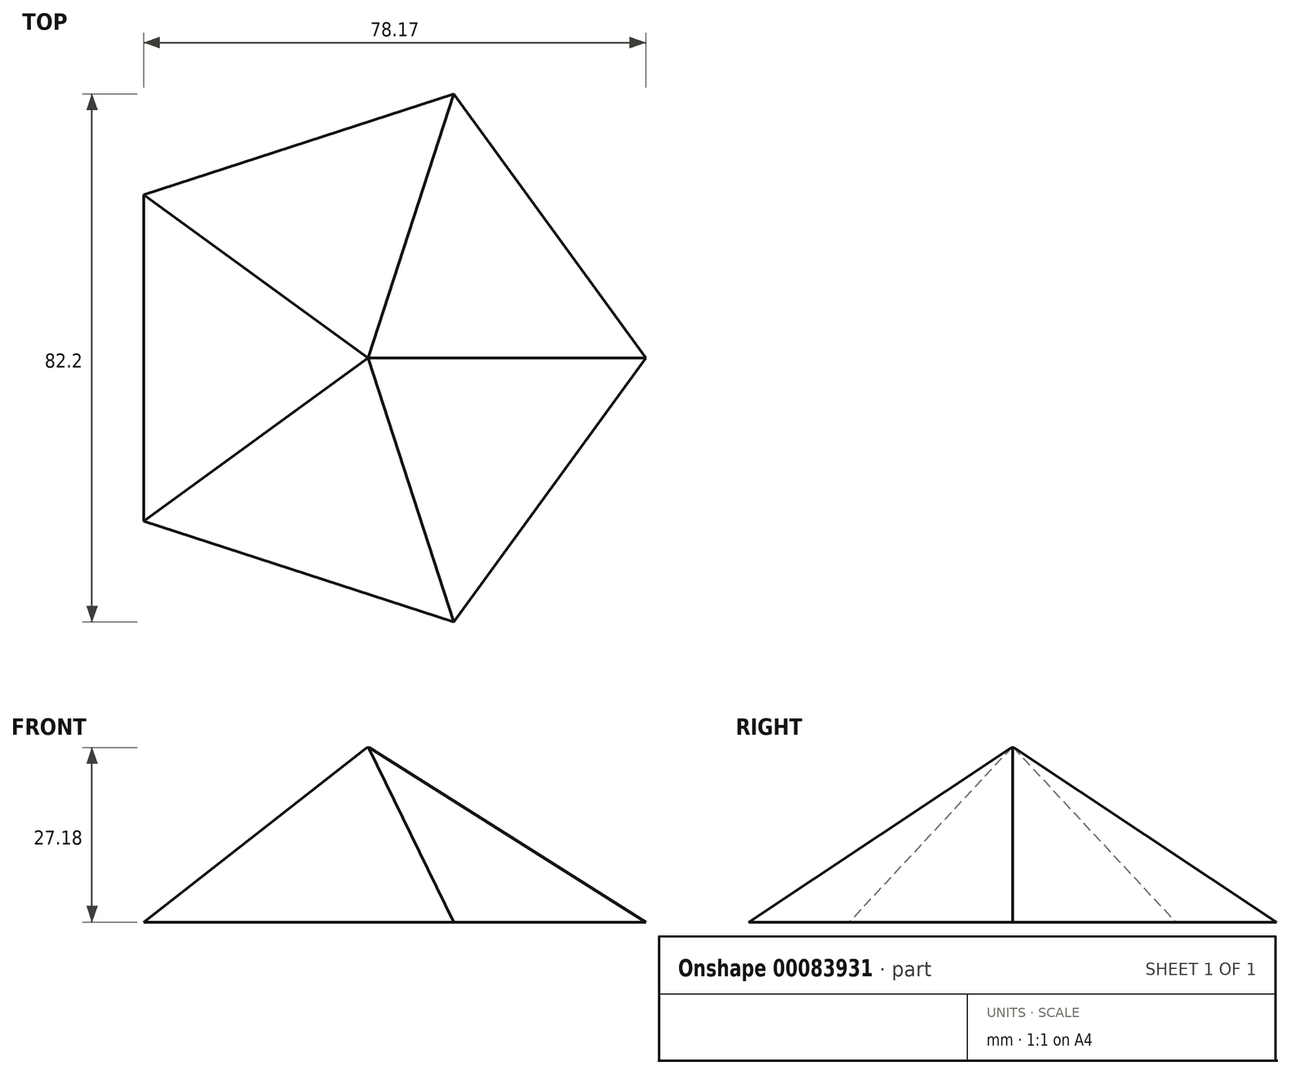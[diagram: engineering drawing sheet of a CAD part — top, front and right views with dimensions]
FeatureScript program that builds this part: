
annotation { "Feature Type Name" : "Feature", "Feature Type Description" : "" }
export const myFeature = defineFeature(function(context is Context, id is Id, definition is map)
    precondition{}
    {
        {
            var Q0;
            Q0=qCreatedBy(makeId("Top.planeOp"),FACE);
            var sketch = newSketch(context, id + "F0", { "sketchPlane" : qUnion([Q0])});
            skCircle(sketch, "E0.cCircle", {"center": v(0, 0) * mm, "radius": 34.96 * mm, "construction": true});
            skLineSegment(sketch, "E0.0", {"start": v(13.35, -41.1) * mm, "end": v(-34.96, -25.4) * mm});
            skLineSegment(sketch, "E0.1", {"start": v(-34.96, -25.4) * mm, "end": v(-34.96, 25.4) * mm});
            skLineSegment(sketch, "E0.2", {"start": v(-34.96, 25.4) * mm, "end": v(13.35, 41.1) * mm});
            skLineSegment(sketch, "E0.3", {"start": v(13.35, 41.1) * mm, "end": v(43.21, 0) * mm});
            skLineSegment(sketch, "E0.4", {"start": v(43.21, 0) * mm, "end": v(13.35, -41.1) * mm});
            skPoint(sketch, "E0.0.midPoint", {"position": v(-10.8, -33.25) * mm});
            skSolve(sketch);
        }
        {
            var Q0;
            Q0 = qSketchRegion(id + "F0", true);
            extrude(context, id + "F1", {"entities" : qUnion([Q0]), "depth" : 27.18 * mm});
        }
        {
            var Q0;
            Q0=makeQuery(id+"F1.opExtrude","CAP_EDGE",EDGE,{"disambiguationData":[OSD([sQuery(id+"F0.wireOp",EDGE,"E0.4")])],"isStart":false});
            var Q1;
            Q1=makeQuery(id+"F1.opExtrude","CAP_FACE",FACE,{"disambiguationData":[OSD([sQuery(id+"F0.wireOp",EDGE,"E0.0"),sQuery(id+"F0.wireOp",EDGE,"E0.1"),sQuery(id+"F0.wireOp",EDGE,"E0.2"),sQuery(id+"F0.wireOp",EDGE,"E0.3"),sQuery(id+"F0.wireOp",EDGE,"E0.4")])],"isStart":false});
            chamfer(context, id + "F2", {"entities" : qUnion([Q0, Q1]), "chamferType" : ChamferType.OFFSET_ANGLE, "width" : 27.18 * mm, "oppositeDirection" : false, "angle" : 52 * degree, "tangentPropagation" : true});
        }
        {
            var Q0;
            Q0=qCreatedBy(makeId("Front.planeOp"),FACE);
            var sketch = newSketch(context, id + "F3", { "sketchPlane" : qUnion([Q0])});
            skLineSegment(sketch, "E1.bottom", {"start": v(-59.2, 35.18) * mm, "end": v(59.03, 35.18) * mm});
            skLineSegment(sketch, "E1.top", {"start": v(-59.2, -33.56) * mm, "end": v(59.03, -33.56) * mm});
            skLineSegment(sketch, "E1.left", {"start": v(-59.2, 35.18) * mm, "end": v(-59.2, -33.56) * mm});
            skLineSegment(sketch, "E1.right", {"start": v(59.03, 35.18) * mm, "end": v(59.03, -33.56) * mm});
            skSolve(sketch);
        }
        {
            var Q0;
            Q0=makeQuery(id+"F2.opChamfer","BLEND_EDGE",EDGE,{"blendedFrom":[makeQuery(id+"F1.opExtrude","CAP_EDGE",EDGE,{"disambiguationData":[OSD([sQuery(id+"F0.wireOp",EDGE,"E0.2")])],"isStart":false}),makeQuery(id+"F1.opExtrude","CAP_EDGE",EDGE,{"disambiguationData":[OSD([sQuery(id+"F0.wireOp",EDGE,"E0.3")])],"isStart":false})],"blendedInto":[]});
            cPlane(context, id + "F4", {"entities" : qUnion([Q0]), "cplaneType" : CPlaneType.MID_PLANE, "offset" : 152.4 * mm, "width" : 152.4 * mm, "height" : 152.4 * mm});
        }
    });
